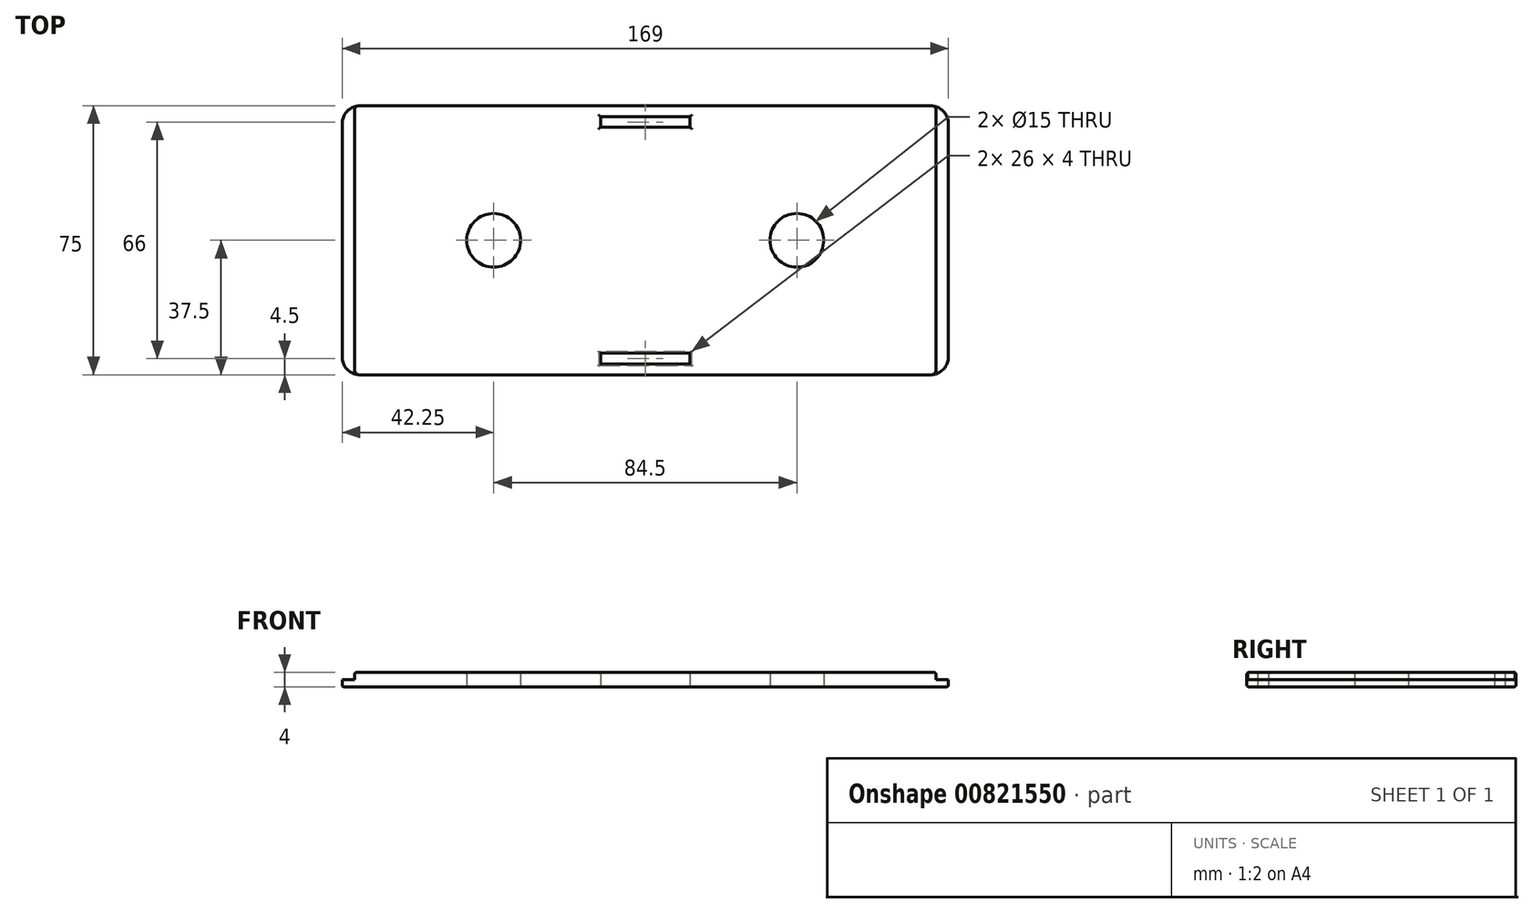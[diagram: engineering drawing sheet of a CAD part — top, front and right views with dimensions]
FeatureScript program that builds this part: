
annotation { "Feature Type Name" : "Feature", "Feature Type Description" : "" }
export const myFeature = defineFeature(function(context is Context, id is Id, definition is map)
    precondition{}
    {
        {
            var Q0;
            Q0=qCreatedBy(makeId("Top.planeOp"),FACE);
            var sketch = newSketch(context, id + "F0", { "sketchPlane" : qUnion([Q0])});
            skLineSegment(sketch, "E0.bottom", {"start": v(84.5, -37.5) * mm, "end": v(-84.5, -37.5) * mm});
            skLineSegment(sketch, "E0.top", {"start": v(84.5, 37.5) * mm, "end": v(-84.5, 37.5) * mm});
            skLineSegment(sketch, "E0.left", {"start": v(84.5, -37.5) * mm, "end": v(84.5, 37.5) * mm});
            skLineSegment(sketch, "E0.right", {"start": v(-84.5, -37.5) * mm, "end": v(-84.5, 37.5) * mm});
            skPoint(sketch, "E0.middle", {"position": v(0, 0) * mm});
            skLineSegment(sketch, "E1", {"start": v(-84.5, 0) * mm, "end": v(0, 0) * mm, "construction": true});
            skCircle(sketch, "E2", {"center": v(-42.25, 0) * mm, "radius": 7.5 * mm});
            skLineSegment(sketch, "E3", {"start": v(0, 0) * mm, "end": v(84.5, 0) * mm, "construction": true});
            skCircle(sketch, "E4", {"center": v(42.25, 0) * mm, "radius": 7.5 * mm});
            skSolve(sketch);
        }
        {
            var Q0;
            Q0=qSketchRegion(id+"F0",true);
            extrude(context, id + "F1", {"entities" : qUnion([Q0]), "depth" : 2 * mm, "offsetDistance" : 25 * mm});
        }
        {
            var Q0;
            Q0=makeQuery(id+"F1.opExtrude","CAP_FACE",FACE,{"disambiguationData":[OSD([sQuery(id+"F0.wireOp",EDGE,"E0.bottom"),sQuery(id+"F0.wireOp",EDGE,"E0.top"),sQuery(id+"F0.wireOp",EDGE,"E0.left"),sQuery(id+"F0.wireOp",EDGE,"E0.right"),sQuery(id+"F0.wireOp",EDGE,"E2"),sQuery(id+"F0.wireOp",EDGE,"E4")])],"isStart":false});
            var sketch = newSketch(context, id + "F2", { "sketchPlane" : qUnion([Q0])});
            skLineSegment(sketch, "E5.bottom", {"start": v(-81, 37.5) * mm, "end": v(81, 37.5) * mm});
            skLineSegment(sketch, "E5.top", {"start": v(-81, -37.5) * mm, "end": v(81, -37.5) * mm});
            skLineSegment(sketch, "E5.left", {"start": v(-81, 37.5) * mm, "end": v(-81, -37.5) * mm});
            skLineSegment(sketch, "E5.right", {"start": v(81, 37.5) * mm, "end": v(81, -37.5) * mm});
            skPoint(sketch, "E5.middle", {"position": v(0, 0) * mm});
            skLineSegment(sketch, "E6.bottom", {"start": v(-12.5, 34.5) * mm, "end": v(12.5, 34.5) * mm});
            skLineSegment(sketch, "E6.top", {"start": v(-12.5, 31.5) * mm, "end": v(12.5, 31.5) * mm});
            skLineSegment(sketch, "E6.left", {"start": v(-12.5, 34.5) * mm, "end": v(-12.5, 31.5) * mm});
            skLineSegment(sketch, "E6.right", {"start": v(12.5, 34.5) * mm, "end": v(12.5, 31.5) * mm});
            skPoint(sketch, "E7", {"position": v(0, 34.5) * mm});
            skLineSegment(sketch, "E8", {"start": v(0, 34.5) * mm, "end": v(0, 37.5) * mm, "construction": true});
            skLineSegment(sketch, "E9.bottom", {"start": v(-12.5, -31.5) * mm, "end": v(12.5, -31.5) * mm});
            skLineSegment(sketch, "E9.top", {"start": v(-12.5, -34.5) * mm, "end": v(12.5, -34.5) * mm});
            skLineSegment(sketch, "E9.left", {"start": v(-12.5, -31.5) * mm, "end": v(-12.5, -34.5) * mm});
            skLineSegment(sketch, "E9.right", {"start": v(12.5, -31.5) * mm, "end": v(12.5, -34.5) * mm});
            skPoint(sketch, "E10", {"position": v(0, -31.5) * mm});
            skLineSegment(sketch, "E11", {"start": v(0, -37.5) * mm, "end": v(0, -34.5) * mm, "construction": true});
            skSolve(sketch);
        }
        {
            var Q0;
            Q0=qSketchRegion(id+"F2",true);
            extrude(context, id + "F3", {"entities" : qUnion([Q0]), "operationType" : NewBodyOperationType.ADD, "depth" : 2 * mm, "offsetDistance" : 25 * mm});
        }
        {
            var Q0;
            Q0=makeQuery(id+"F1.opExtrude","SWEPT_EDGE",EDGE,{"disambiguationData":[OSD([sQuery(id+"F0.wireOp",EDGE,"E0.bottom"),sQuery(id+"F0.wireOp",EDGE,"E0.right")])]});
            var Q1;
            Q1=makeQuery(id+"F1.opExtrude","SWEPT_EDGE",EDGE,{"disambiguationData":[OSD([sQuery(id+"F0.wireOp",EDGE,"E0.bottom"),sQuery(id+"F0.wireOp",EDGE,"E0.left")])]});
            var Q2;
            Q2=makeQuery(id+"F1.opExtrude","SWEPT_EDGE",EDGE,{"disambiguationData":[OSD([sQuery(id+"F0.wireOp",EDGE,"E0.top"),sQuery(id+"F0.wireOp",EDGE,"E0.left")])]});
            var Q3;
            Q3=makeQuery(id+"F1.opExtrude","SWEPT_EDGE",EDGE,{"disambiguationData":[OSD([sQuery(id+"F0.wireOp",EDGE,"E0.top"),sQuery(id+"F0.wireOp",EDGE,"E0.right")])]});
            fillet(context, id + "F4", {"entities" : qUnion([Q0, Q1, Q2, Q3]), "radius" : 5 * mm, "tangentPropagation" : true, "allowEdgeOverflow" : false});
        }
        {
            var Q0;
            Q0=makeQuery(id+"F0.imprint","IMPRINT",FACE,{"disambiguationData":[TD([[makeQuery(id+"F0.imprint","IMPRINT",EDGE,{"derivedFrom":sQuery(id+"F0.wireOp",EDGE,"E4")}),1.0]])]});
            var Q1;
            Q1=makeQuery(id+"F0.imprint","IMPRINT",FACE,{"disambiguationData":[TD([[makeQuery(id+"F0.imprint","IMPRINT",EDGE,{"derivedFrom":sQuery(id+"F0.wireOp",EDGE,"E2")}),1.0]])]});
            extrude(context, id + "F5", {"entities" : qUnion([Q0, Q1]), "operationType" : NewBodyOperationType.REMOVE, "depth" : 25 * mm, "offsetDistance" : 25 * mm});
        }
        {
            var Q0;
            Q0=makeQuery(id+"F2.imprint","IMPRINT",FACE,{"disambiguationData":[TD([[makeQuery(id+"F2.imprint","IMPRINT",EDGE,{"derivedFrom":sQuery(id+"F2.wireOp",EDGE,"E6.bottom")}),-1.0]])]});
            var Q1;
            Q1=makeQuery(id+"F2.imprint","IMPRINT",FACE,{"disambiguationData":[TD([[makeQuery(id+"F2.imprint","IMPRINT",EDGE,{"derivedFrom":sQuery(id+"F2.wireOp",EDGE,"E9.bottom")}),-1.0]])]});
            extrude(context, id + "F6", {"entities" : qUnion([Q0, Q1]), "operationType" : NewBodyOperationType.REMOVE, "oppositeDirection" : true, "depth" : 25 * mm, "offsetDistance" : 25 * mm});
        }
        {
            var Q0;
            Q0=makeQuery(id+"F3.opExtrude","CAP_FACE",FACE,{"disambiguationData":[OSD([sQuery(id+"F2.wireOp",EDGE,"E5.bottom"),sQuery(id+"F2.wireOp",EDGE,"E5.top"),sQuery(id+"F2.wireOp",EDGE,"E5.left"),sQuery(id+"F2.wireOp",EDGE,"E5.right"),sQuery(id+"F2.wireOp",EDGE,"E6.bottom"),sQuery(id+"F2.wireOp",EDGE,"E6.top"),sQuery(id+"F2.wireOp",EDGE,"E6.left"),sQuery(id+"F2.wireOp",EDGE,"E6.right"),sQuery(id+"F2.wireOp",EDGE,"E9.bottom"),sQuery(id+"F2.wireOp",EDGE,"E9.top"),sQuery(id+"F2.wireOp",EDGE,"E9.left"),sQuery(id+"F2.wireOp",EDGE,"E9.right")])],"isStart":false});
            var Q1;
            Q1=makeQuery(id+"F1.opExtrude","CAP_FACE",FACE,{"disambiguationData":[OSD([sQuery(id+"F0.wireOp",EDGE,"E0.bottom"),sQuery(id+"F0.wireOp",EDGE,"E0.top"),sQuery(id+"F0.wireOp",EDGE,"E0.left"),sQuery(id+"F0.wireOp",EDGE,"E0.right"),sQuery(id+"F0.wireOp",EDGE,"E2"),sQuery(id+"F0.wireOp",EDGE,"E4")])],"isStart":true});
            fillet(context, id + "F7", {"entities" : qUnion([Q0, Q1]), "radius" : .5 * mm, "tangentPropagation" : true, "allowEdgeOverflow" : false});
        }
    });
